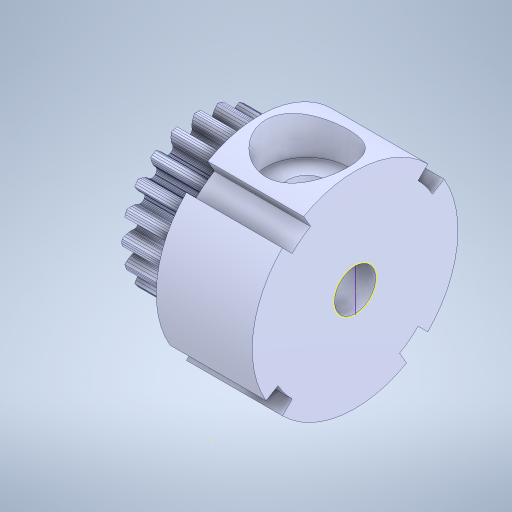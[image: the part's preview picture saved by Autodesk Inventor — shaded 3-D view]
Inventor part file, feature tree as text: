
AUTODESK INVENTOR PART (.ipt)
format: ipt  version: 2023.5 (Build 275446000, 446)  size: 2,206,208 bytes
history: native  units: mm
features: sketch x7, extrude x5, other x4, projected_geometry x3, pattern_circular x1, hole x1, mirror x1
ambient origin geometry x8: Origin, YZ Plane, XZ Plane, XY Plane, X Axis, Y Axis, Z Axis, Center Point
bodies: Body1 (feature_tree)
feature tree (22):
  extrude  "Wyciągnięcie proste1"  Depth=15.0mm
  extrude  "Wyciągnięcie proste2"  Depth=7.0mm TaperAngle=0.0deg
  sketch  "Szkic3"
  other  "Płaszczyzna konstrukcyjna2"
  extrude  "Wyciągnięcie proste3"  Depth=1.0mm TaperAngle=0.0deg
  pattern_circular  "Szyk kołowy1"  [2 undecoded]
  extrude  "Wyciągnięcie proste4"  TaperAngle=15.0deg  [1 undecoded]
  hole  "Otwór1"  [1 undecoded]
  mirror  "Odbij1"
  extrude  "Wyciągnięcie proste5"  TaperAngle=0.0deg  [1 undecoded]
  other  "Bryła31"
  sketch  "Szkic1"
  sketch  "Szkic2"
  projected_geometry  "Pętla rzutowana1"
  other  "Płaszczyzna konstrukcyjna1"
  sketch  "Szkic5"
  sketch  "Szkic6"
  projected_geometry  "Pętla rzutowana2"
  sketch  "Szkic7"
  sketch  "Szkic8"
  projected_geometry  "Pętla rzutowana3"
  other  "Engrane_8:1"
note: 5 required parameter values undecoded (feature->parameter linkage not recoverable at this tier; creation-order binding heuristic only, values carry confidence <= 0.55)
